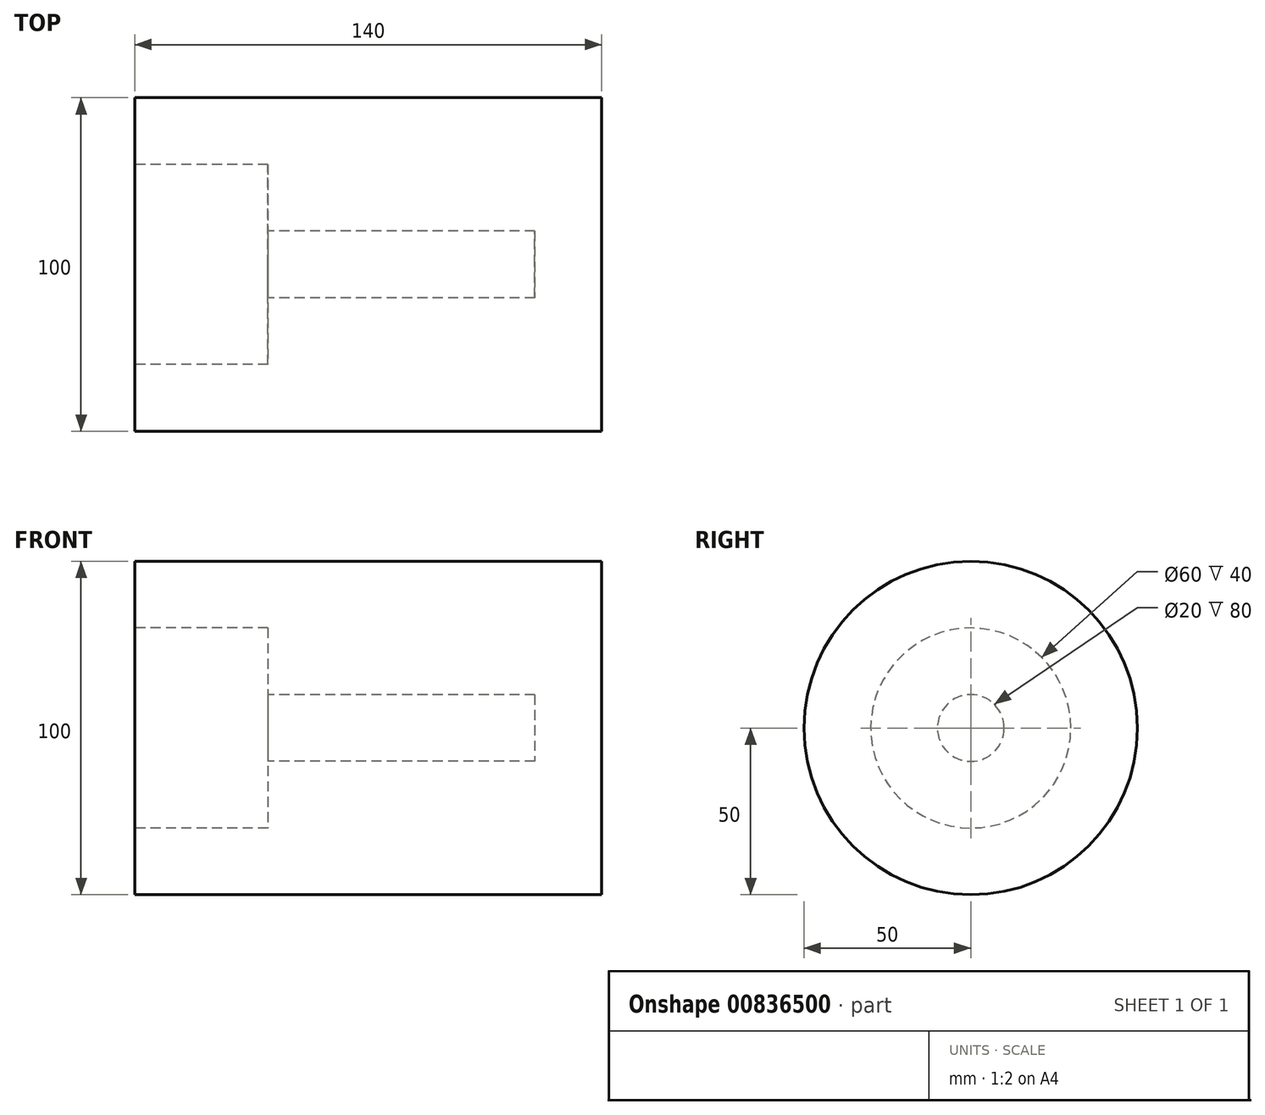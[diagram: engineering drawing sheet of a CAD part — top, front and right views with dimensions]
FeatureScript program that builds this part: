
annotation { "Feature Type Name" : "Feature", "Feature Type Description" : "" }
export const myFeature = defineFeature(function(context is Context, id is Id, definition is map)
    precondition{}
    {
        {
            var Q0;
            Q0=qCreatedBy(makeId("Top.planeOp"),FACE);
            var sketch = newSketch(context, id + "F0", { "sketchPlane" : qUnion([Q0])});
            skLineSegment(sketch, "E0.bottom", {"start": v(0, 0) * mm, "end": v(140, 0) * mm});
            skLineSegment(sketch, "E0.top", {"start": v(0, 50) * mm, "end": v(140, 50) * mm});
            skLineSegment(sketch, "E0.left", {"start": v(0, 30) * mm, "end": v(0, 50) * mm});
            skLineSegment(sketch, "E0.right", {"start": v(140, 0) * mm, "end": v(140, 50) * mm});
            skLineSegment(sketch, "E1.top", {"start": v(40, 10) * mm, "end": v(120, 10) * mm});
            skLineSegment(sketch, "E1.right", {"start": v(120, 0) * mm, "end": v(120, 10) * mm});
            skLineSegment(sketch, "E2.top", {"start": v(0, 30) * mm, "end": v(40, 30) * mm});
            skLineSegment(sketch, "E2.right", {"start": v(40, 10) * mm, "end": v(40, 30) * mm});
            skSolve(sketch);
        }
        {
            var Q0;
            Q0=makeQuery(id+"F0.imprint","IMPRINT",FACE,{"disambiguationData":[TD([[makeQuery(id+"F0.imprint","IMPRINT",EDGE,{"derivedFrom":sQuery(id+"F0.wireOp",EDGE,"E0.top")}),-1.0]])]});
            var Q1;
            Q1=sQuery(id+"F0.wireOp",EDGE,"E0.bottom");
            revolve(context, id + "F1", {"surfaceOperationType" : NewSurfaceOperationType.NEW, "entities" : qUnion([Q0]), "axis" : qUnion([Q1]), "revolveType" : RevolveType.FULL});
        }
    });
